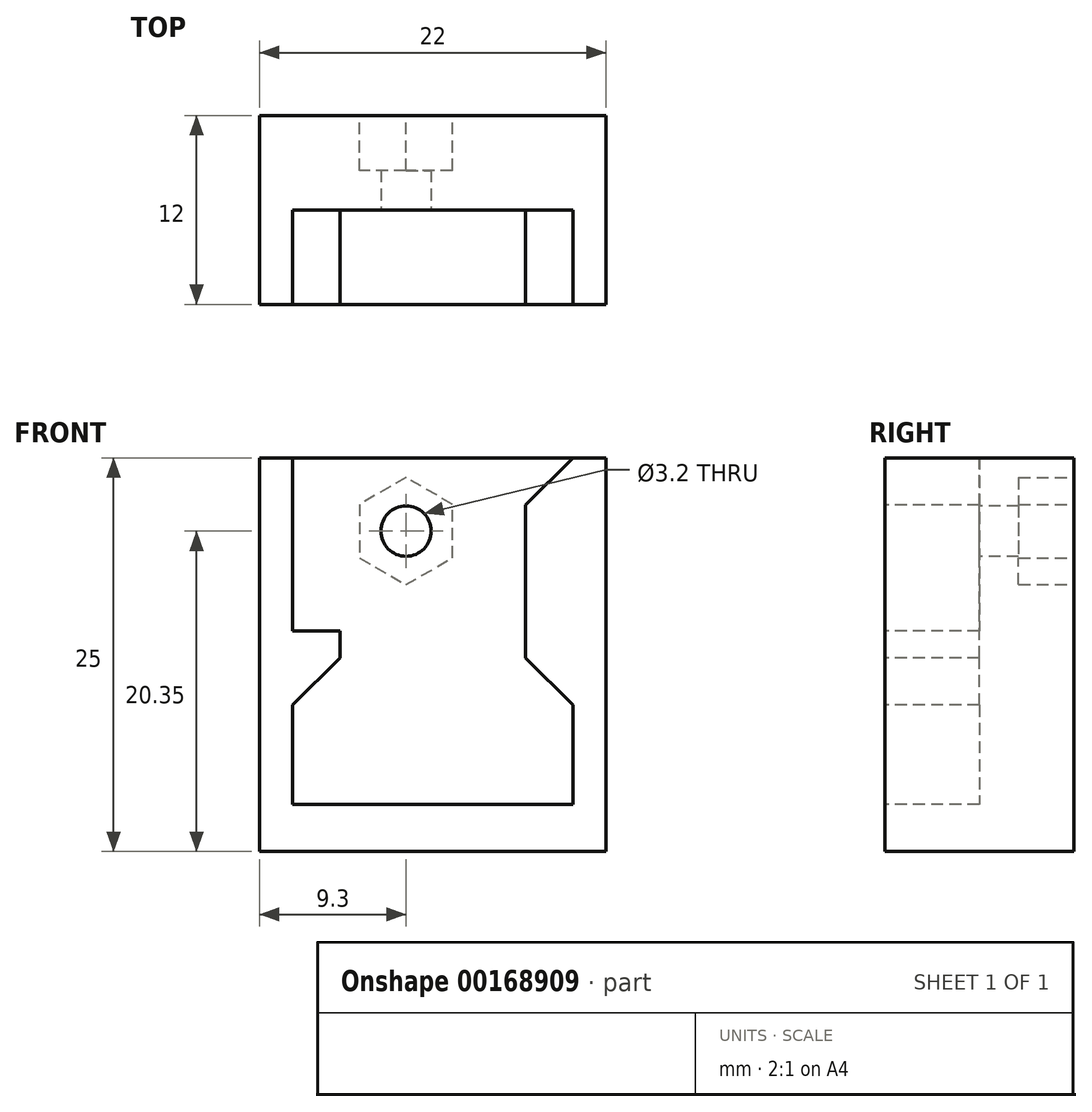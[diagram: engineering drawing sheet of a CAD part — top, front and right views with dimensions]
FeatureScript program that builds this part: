
annotation { "Feature Type Name" : "Feature", "Feature Type Description" : "" }
export const myFeature = defineFeature(function(context is Context, id is Id, definition is map)
    precondition{}
    {
        {
            var Q0;
            Q0=qCreatedBy(makeId("Front.planeOp"),FACE);
            var sketch = newSketch(context, id + "F0", { "sketchPlane" : qUnion([Q0])});
            skLineSegment(sketch, "E0.bottom", {"start": v(-11, 25) * mm, "end": v(11, 25) * mm});
            skLineSegment(sketch, "E0.top", {"start": v(-11, 0) * mm, "end": v(11, 0) * mm});
            skLineSegment(sketch, "E0.left", {"start": v(-11, 25) * mm, "end": v(-11, 0) * mm});
            skLineSegment(sketch, "E0.right", {"start": v(11, 25) * mm, "end": v(11, 0) * mm});
            skSolve(sketch);
        }
        {
            var Q0;
            Q0=makeQuery(id+"F0.imprint","IMPRINT",FACE,{"disambiguationData":[TD([[makeQuery(id+"F0.imprint","IMPRINT",EDGE,{"derivedFrom":sQuery(id+"F0.wireOp",EDGE,"E0.bottom")}),-1.0]])]});
            extrude(context, id + "F1", {"entities" : qUnion([Q0]), "oppositeDirection" : true, "depth" : 12 * mm});
        }
        {
            var Q0;
            Q0=makeQuery(id+"F1.opExtrude","CAP_FACE",FACE,{"disambiguationData":[OSD([sQuery(id+"F0.wireOp",EDGE,"E0.bottom"),sQuery(id+"F0.wireOp",EDGE,"E0.top"),sQuery(id+"F0.wireOp",EDGE,"E0.left"),sQuery(id+"F0.wireOp",EDGE,"E0.right")])],"isStart":true});
            var sketch = newSketch(context, id + "F2", { "sketchPlane" : qUnion([Q0])});
            skLineSegment(sketch, "E1.bottom", {"start": v(-8.9, 25) * mm, "end": v(8.9, 25) * mm});
            skLineSegment(sketch, "E1.top", {"start": v(-8.9, 3) * mm, "end": v(8.9, 3) * mm});
            skLineSegment(sketch, "E1.left", {"start": v(-8.9, 25) * mm, "end": v(-8.9, 3) * mm});
            skLineSegment(sketch, "E1.right", {"start": v(8.9, 25) * mm, "end": v(8.9, 3) * mm});
            skLineSegment(sketch, "E2", {"start": v(0, 25) * mm, "end": v(0, 0) * mm, "construction": true});
            skSolve(sketch);
        }
        {
            var Q0;
            Q0=makeQuery(id+"F2.imprint","IMPRINT",FACE,{"disambiguationData":[TD([[makeQuery(id+"F2.imprint","IMPRINT",EDGE,{"derivedFrom":sQuery(id+"F2.wireOp",EDGE,"E1.bottom")}),-1.0]])]});
            extrude(context, id + "F3", {"entities" : qUnion([Q0]), "operationType" : NewBodyOperationType.REMOVE, "oppositeDirection" : true, "depth" : 6 * mm});
        }
        {
            var Q0;
            Q0=makeQuery(id+"F1.opExtrude","CAP_FACE",FACE,{"disambiguationData":[OSD([sQuery(id+"F0.wireOp",EDGE,"E0.bottom"),sQuery(id+"F0.wireOp",EDGE,"E0.top"),sQuery(id+"F0.wireOp",EDGE,"E0.left"),sQuery(id+"F0.wireOp",EDGE,"E0.right")])],"isStart":true});
            var sketch = newSketch(context, id + "F4", { "sketchPlane" : qUnion([Q0])});
            skLineSegment(sketch, "E3", {"start": v(-8.9, 14) * mm, "end": v(-5.9, 14) * mm});
            skLineSegment(sketch, "E4", {"start": v(-5.9, 14) * mm, "end": v(-5.9, 12.3) * mm});
            skLineSegment(sketch, "E5", {"start": v(-5.9, 12.3) * mm, "end": v(-8.9, 9.3) * mm});
            skLineSegment(sketch, "E6", {"start": v(-8.9, 9.3) * mm, "end": v(-8.9, 14) * mm});
            skLineSegment(sketch, "E7", {"start": v(8.9, 25) * mm, "end": v(5.9, 22) * mm});
            skLineSegment(sketch, "E8", {"start": v(5.9, 22) * mm, "end": v(5.9, 12.3) * mm});
            skLineSegment(sketch, "E9", {"start": v(5.9, 12.3) * mm, "end": v(8.9, 9.3) * mm});
            skLineSegment(sketch, "E10", {"start": v(8.9, 9.3) * mm, "end": v(8.9, 25) * mm});
            skLineSegment(sketch, "E11", {"start": v(0, 0) * mm, "end": v(0, 23.04) * mm, "construction": true});
            skSolve(sketch);
        }
        {
            var Q0;
            Q0=makeQuery(id+"F4.imprint","IMPRINT",FACE,{"disambiguationData":[TD([[makeQuery(id+"F4.imprint","IMPRINT",EDGE,{"derivedFrom":sQuery(id+"F4.wireOp",EDGE,"E3")}),-1.0]])]});
            var Q1;
            Q1=makeQuery(id+"F4.imprint","IMPRINT",FACE,{"disambiguationData":[TD([[makeQuery(id+"F4.imprint","IMPRINT",EDGE,{"derivedFrom":sQuery(id+"F4.wireOp",EDGE,"E7")}),1.0]])]});
            var Q2;
            Q2=makeQuery(id+"F3.boolean.opBoolean","COPY",FACE,{"derivedFrom":makeQuery(id+"F3.opExtrude","CAP_FACE",FACE,{"disambiguationData":[OSD([sQuery(id+"F2.wireOp",EDGE,"E1.bottom"),sQuery(id+"F2.wireOp",EDGE,"E1.top"),sQuery(id+"F2.wireOp",EDGE,"E1.left"),sQuery(id+"F2.wireOp",EDGE,"E1.right")])],"isStart":false})});
            extrude(context, id + "F5", {"entities" : qUnion([Q0, Q1]), "operationType" : NewBodyOperationType.ADD, "endBound" : BoundingType.UP_TO_SURFACE, "oppositeDirection" : true, "endBoundEntityFace" : qUnion([Q2]), "depth" : 25 * mm});
        }
        {
            var Q0;
            Q0=makeQuery(id+"F3.boolean.opBoolean","COPY",FACE,{"derivedFrom":makeQuery(id+"F3.opExtrude","CAP_FACE",FACE,{"disambiguationData":[OSD([sQuery(id+"F2.wireOp",EDGE,"E1.bottom"),sQuery(id+"F2.wireOp",EDGE,"E1.top"),sQuery(id+"F2.wireOp",EDGE,"E1.left"),sQuery(id+"F2.wireOp",EDGE,"E1.right")])],"isStart":false})});
            var sketch = newSketch(context, id + "F6", { "sketchPlane" : qUnion([Q0])});
            skCircle(sketch, "E12", {"center": v(-1.7, 20.35) * mm, "radius": 1.6 * mm});
            skSolve(sketch);
        }
        {
            var Q0;
            Q0=makeQuery(id+"F6.imprint","IMPRINT",FACE,{"disambiguationData":[TD([[makeQuery(id+"F6.imprint","IMPRINT",EDGE,{"derivedFrom":sQuery(id+"F6.wireOp",EDGE,"E12")}),1.0]])]});
            extrude(context, id + "F7", {"entities" : qUnion([Q0]), "operationType" : NewBodyOperationType.REMOVE, "endBound" : BoundingType.THROUGH_ALL, "oppositeDirection" : true, "depth" : 25 * mm});
        }
        {
            var Q0;
            Q0=makeQuery(id+"F1.opExtrude","CAP_FACE",FACE,{"disambiguationData":[OSD([sQuery(id+"F0.wireOp",EDGE,"E0.bottom"),sQuery(id+"F0.wireOp",EDGE,"E0.top"),sQuery(id+"F0.wireOp",EDGE,"E0.left"),sQuery(id+"F0.wireOp",EDGE,"E0.right")])],"isStart":false});
            var sketch = newSketch(context, id + "F8", { "sketchPlane" : qUnion([Q0])});
            skCircle(sketch, "E13.cCircle", {"center": v(1.7, 20.35) * mm, "radius": 2.95 * mm, "construction": true});
            skLineSegment(sketch, "E13.0", {"start": v(4.65, 22.05) * mm, "end": v(4.65, 18.65) * mm});
            skLineSegment(sketch, "E13.1", {"start": v(4.65, 18.65) * mm, "end": v(1.7, 16.94) * mm});
            skLineSegment(sketch, "E13.2", {"start": v(1.7, 16.94) * mm, "end": v(-1.25, 18.65) * mm});
            skLineSegment(sketch, "E13.3", {"start": v(-1.25, 18.65) * mm, "end": v(-1.25, 22.05) * mm});
            skLineSegment(sketch, "E13.4", {"start": v(-1.25, 22.05) * mm, "end": v(1.7, 23.76) * mm});
            skLineSegment(sketch, "E13.5", {"start": v(1.7, 23.76) * mm, "end": v(4.65, 22.05) * mm});
            skPoint(sketch, "E13.0.midPoint", {"position": v(4.65, 20.35) * mm});
            skSolve(sketch);
        }
        {
            var Q0;
            Q0 = qSketchRegion(id + "F8", true);
            extrude(context, id + "F9", {"entities" : qUnion([Q0]), "operationType" : NewBodyOperationType.REMOVE, "oppositeDirection" : true, "depth" : 3.5 * mm});
        }
    });
